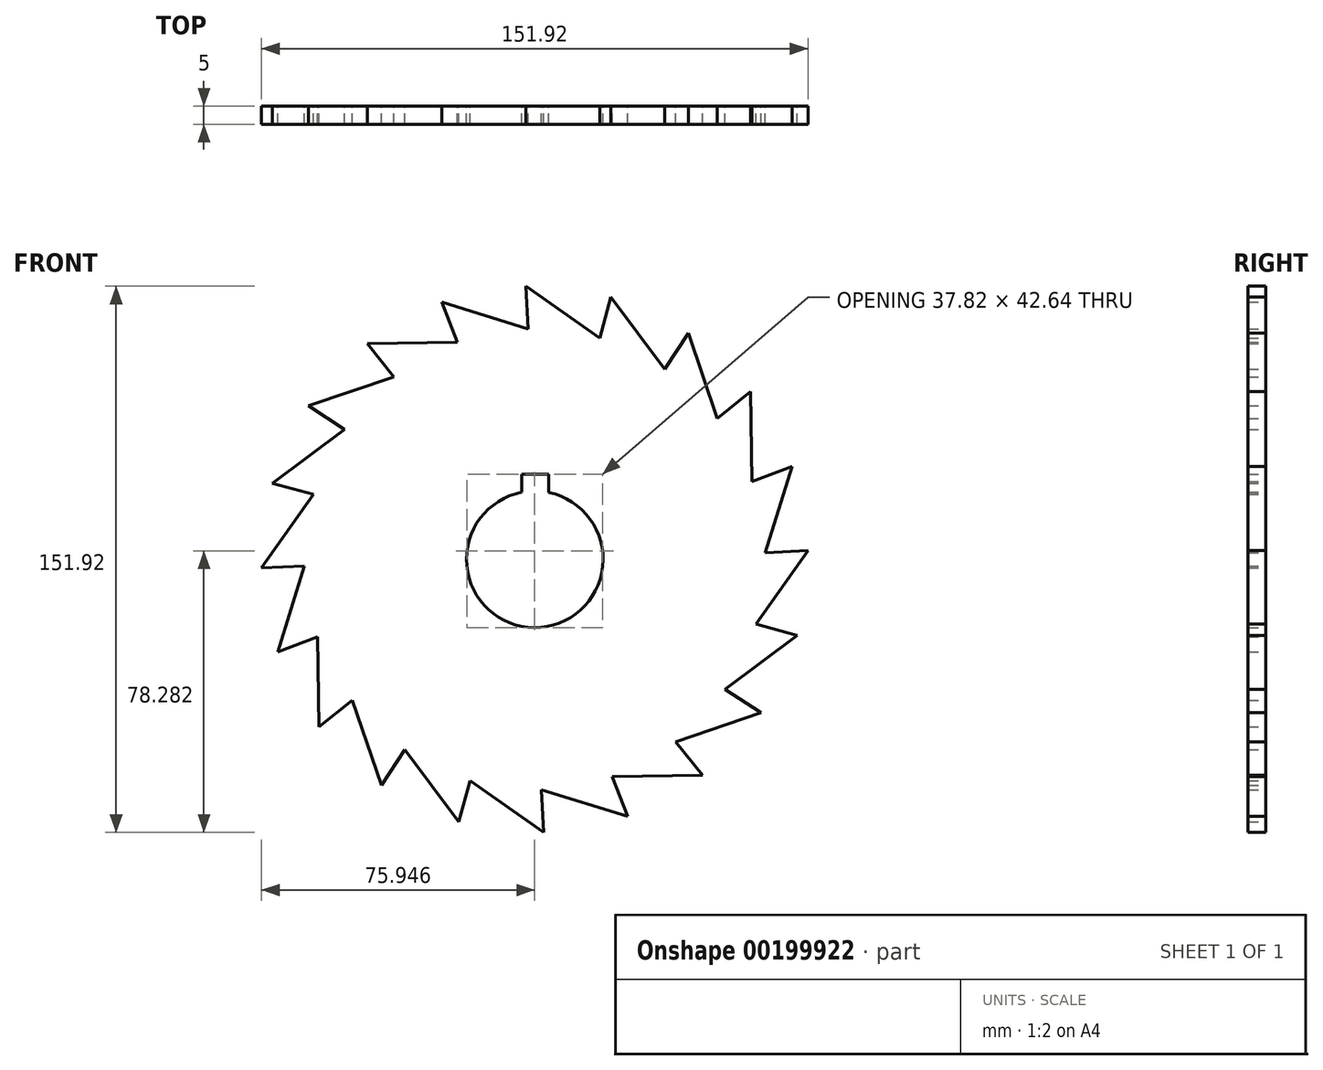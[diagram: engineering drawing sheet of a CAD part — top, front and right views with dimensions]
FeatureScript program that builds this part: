
annotation { "Feature Type Name" : "Feature", "Feature Type Description" : "" }
export const myFeature = defineFeature(function(context is Context, id is Id, definition is map)
    precondition{}
    {
        {
            var Q0;
            Q0=qCreatedBy(makeId("Front.planeOp"),FACE);
            var sketch = newSketch(context, id + "F0", { "sketchPlane" : qUnion([Q0])});
            skCircle(sketch, "E0", {"center": v(0, 0) * mm, "radius": 19 * mm});
            skCircle(sketch, "E1", {"center": v(0, 0) * mm, "radius": 76 * mm});
            skLineSegment(sketch, "E2", {"start": v(63.5, 0) * mm, "end": v(71.5, 25.8) * mm});
            skLineSegment(sketch, "E3", {"start": v(71.5, 25.8) * mm, "end": v(59.8, 21.35) * mm});
            skLineSegment(sketch, "E4.1.0", {"start": v(60.02, 46.62) * mm, "end": v(50.28, 38.79) * mm});
            skLineSegment(sketch, "E4.1.1", {"start": v(60.4, 19.62) * mm, "end": v(60.02, 46.62) * mm});
            skLineSegment(sketch, "E4.2.0", {"start": v(42.68, 62.89) * mm, "end": v(35.83, 52.43) * mm});
            skLineSegment(sketch, "E4.2.1", {"start": v(51.37, 37.32) * mm, "end": v(42.68, 62.89) * mm});
            skLineSegment(sketch, "E4.3.0", {"start": v(21.16, 73) * mm, "end": v(17.88, 60.93) * mm});
            skLineSegment(sketch, "E4.3.1", {"start": v(37.32, 51.37) * mm, "end": v(21.16, 73) * mm});
            skLineSegment(sketch, "E4.4.0", {"start": v(-2.44, 75.96) * mm, "end": v(-1.83, 63.47) * mm});
            skLineSegment(sketch, "E4.4.1", {"start": v(19.62, 60.4) * mm, "end": v(-2.44, 75.96) * mm});
            skLineSegment(sketch, "E4.5.0", {"start": v(-25.8, 71.5) * mm, "end": v(-21.35, 59.8) * mm});
            skLineSegment(sketch, "E4.5.1", {"start": v(0, 63.5) * mm, "end": v(-25.8, 71.5) * mm});
            skLineSegment(sketch, "E4.6.0", {"start": v(-46.62, 60.02) * mm, "end": v(-38.79, 50.28) * mm});
            skLineSegment(sketch, "E4.6.1", {"start": v(-19.62, 60.4) * mm, "end": v(-46.62, 60.02) * mm});
            skLineSegment(sketch, "E4.7.0", {"start": v(-62.89, 42.68) * mm, "end": v(-52.43, 35.83) * mm});
            skLineSegment(sketch, "E4.7.1", {"start": v(-37.32, 51.37) * mm, "end": v(-62.89, 42.68) * mm});
            skLineSegment(sketch, "E4.8.0", {"start": v(-73, 21.16) * mm, "end": v(-60.93, 17.88) * mm});
            skLineSegment(sketch, "E4.8.1", {"start": v(-51.37, 37.32) * mm, "end": v(-73, 21.16) * mm});
            skLineSegment(sketch, "E4.9.0", {"start": v(-75.96, -2.44) * mm, "end": v(-63.47, -1.83) * mm});
            skLineSegment(sketch, "E4.9.1", {"start": v(-60.4, 19.62) * mm, "end": v(-75.96, -2.44) * mm});
            skLineSegment(sketch, "E4.10.0", {"start": v(-71.5, -25.8) * mm, "end": v(-59.8, -21.35) * mm});
            skLineSegment(sketch, "E4.10.1", {"start": v(-63.5, 0) * mm, "end": v(-71.5, -25.8) * mm});
            skLineSegment(sketch, "E4.11.0", {"start": v(-60.02, -46.62) * mm, "end": v(-50.28, -38.79) * mm});
            skLineSegment(sketch, "E4.11.1", {"start": v(-60.4, -19.62) * mm, "end": v(-60.02, -46.62) * mm});
            skLineSegment(sketch, "E4.12.0", {"start": v(-42.68, -62.89) * mm, "end": v(-35.83, -52.43) * mm});
            skLineSegment(sketch, "E4.12.1", {"start": v(-51.37, -37.32) * mm, "end": v(-42.68, -62.89) * mm});
            skLineSegment(sketch, "E4.13.0", {"start": v(-21.16, -73) * mm, "end": v(-17.88, -60.93) * mm});
            skLineSegment(sketch, "E4.13.1", {"start": v(-37.32, -51.37) * mm, "end": v(-21.16, -73) * mm});
            skLineSegment(sketch, "E4.14.0", {"start": v(2.44, -75.96) * mm, "end": v(1.83, -63.47) * mm});
            skLineSegment(sketch, "E4.14.1", {"start": v(-19.62, -60.4) * mm, "end": v(2.44, -75.96) * mm});
            skLineSegment(sketch, "E4.15.0", {"start": v(25.8, -71.5) * mm, "end": v(21.35, -59.8) * mm});
            skLineSegment(sketch, "E4.15.1", {"start": v(0, -63.5) * mm, "end": v(25.8, -71.5) * mm});
            skLineSegment(sketch, "E4.16.0", {"start": v(46.62, -60.02) * mm, "end": v(38.79, -50.28) * mm});
            skLineSegment(sketch, "E4.16.1", {"start": v(19.62, -60.4) * mm, "end": v(46.62, -60.02) * mm});
            skLineSegment(sketch, "E4.17.0", {"start": v(62.89, -42.68) * mm, "end": v(52.43, -35.83) * mm});
            skLineSegment(sketch, "E4.17.1", {"start": v(37.32, -51.37) * mm, "end": v(62.89, -42.68) * mm});
            skLineSegment(sketch, "E4.18.0", {"start": v(73, -21.16) * mm, "end": v(60.93, -17.88) * mm});
            skLineSegment(sketch, "E4.18.1", {"start": v(51.37, -37.32) * mm, "end": v(73, -21.16) * mm});
            skLineSegment(sketch, "E4.19.0", {"start": v(75.96, 2.44) * mm, "end": v(63.47, 1.83) * mm});
            skLineSegment(sketch, "E4.19.1", {"start": v(60.4, -19.62) * mm, "end": v(75.96, 2.44) * mm});
            skLineSegment(sketch, "E5.bottom", {"start": v(-3.57, 23.64) * mm, "end": v(3.85, 23.64) * mm});
            skLineSegment(sketch, "E5.top", {"start": v(-3.57, 14.07) * mm, "end": v(3.85, 14.07) * mm});
            skLineSegment(sketch, "E5.left", {"start": v(-3.57, 23.64) * mm, "end": v(-3.57, 14.07) * mm});
            skLineSegment(sketch, "E5.right", {"start": v(3.85, 23.64) * mm, "end": v(3.85, 14.07) * mm});
            skSolve(sketch);
        }
        {
            var Q0;
            {var subQ75=sQuery(id+"F0.wireOp",EDGE,"E5.bottom");Q0=makeQuery(id+"F0.imprint","IMPRINT",FACE,{"disambiguationData":[TD([[makeQuery(id+"F0.imprint","IMPRINT",EDGE,{"derivedFrom":subQ75}),1.0]])]});}
            extrude(context, id + "F1", {"entities" : qUnion([Q0]), "depth" : 5 * mm});
        }
    });
